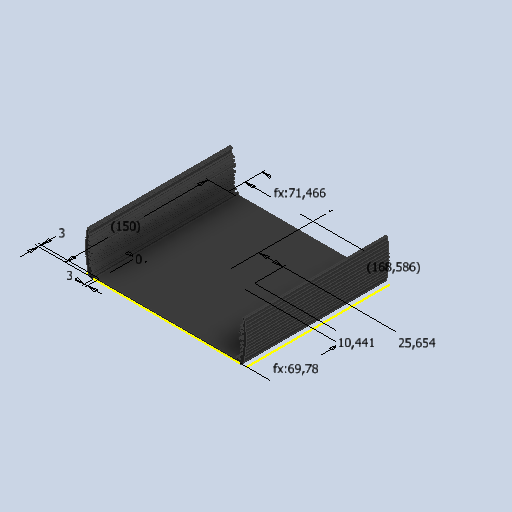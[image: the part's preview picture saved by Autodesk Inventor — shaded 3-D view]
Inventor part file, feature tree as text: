
AUTODESK INVENTOR PART (.ipt)
format: ipt  version: 2024.2 (Build 282272000, 272)  size: 428,544 bytes
history: native  units: mm
features: other x5, sketch x1, reference x1
ambient origin geometry x8: Origin, YZ Plane, XZ Plane, XY Plane, X Axis, Y Axis, Z Axis, Center Point
bodies: Solid1 (feature_tree), Volumenkörper1 (feature_tree)
feature tree (7):
  sketch  "Sketch1"  dims[d0=0.0mm d1=3.0mm d2=3.0mm d3=10.440924mm d4=69.779538mm d5=150.0mm d6=25.654376mm d7=168.586321mm d8=71.465973mm]
  reference  "Reference1"
  other  "<userpath>\Google Drive\Unicorn 2020\CAD_V2\Main_Assembly.iam"
  other  "Main_Assembly.iam"
  other  "Front_Panel_Assembly:1"
  other  "Front_Pane_Basel_Assembly:1"
  other  "DI 1600:1"
